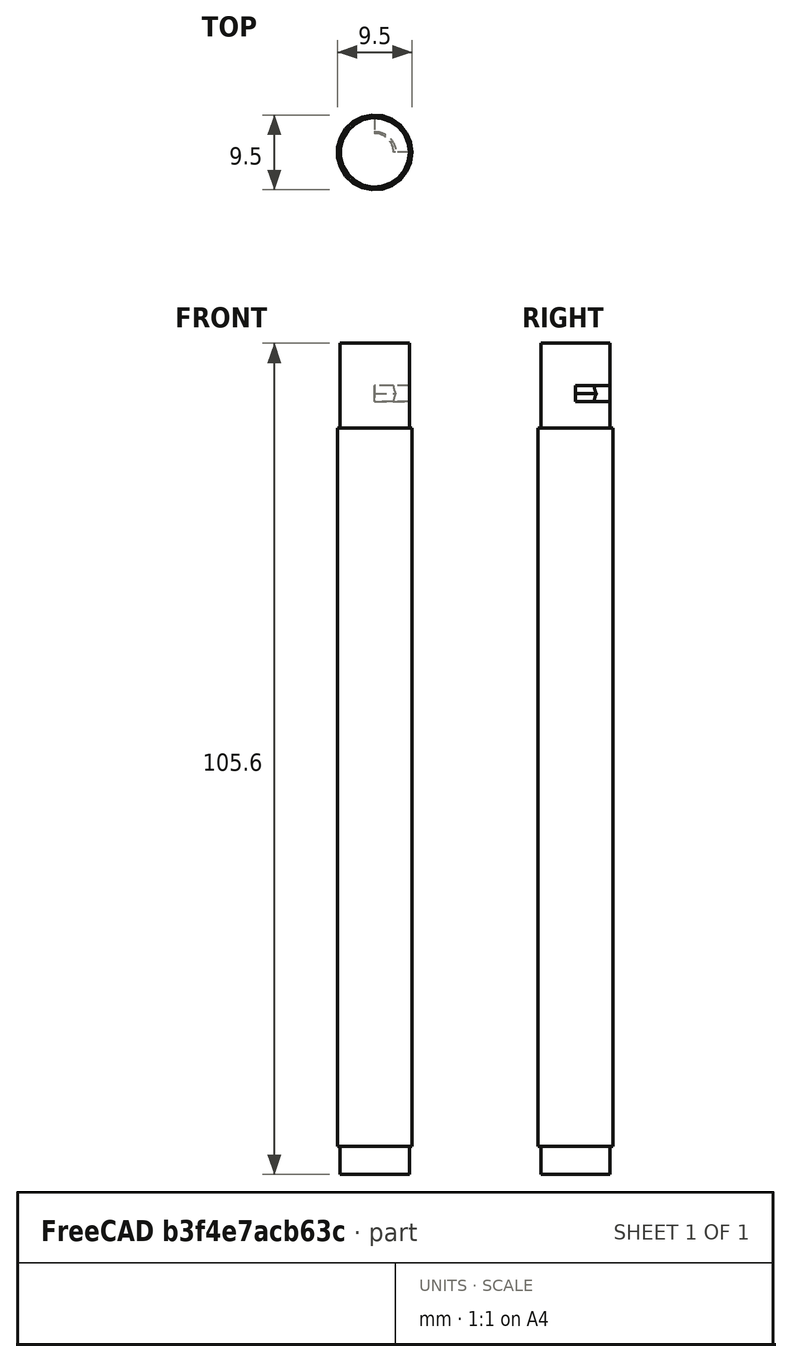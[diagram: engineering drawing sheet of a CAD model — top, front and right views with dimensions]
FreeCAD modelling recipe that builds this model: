
FCSTD DOCUMENT  (FreeCAD 0.20R29603 (Git))
Label: new_shaft
License: All rights reserved
LicenseURL: http://en.wikipedia.org/wiki/All_rights_reserved
objects: PartDesign::AdditiveCylinder×3, PartDesign::SubtractiveTorus×2, PartDesign::Body×1
note: 11 computed .brp shape members not serialized (recipe doc carries the construction recipe); baked Part::Feature solids carry a one-line shape summary decoded from their .brp

FEATURE [PartDesign::AdditiveCylinder] Cylinder
  Angle = 360
  AttacherType = Attacher::AttachEngine3D
  FirstAngle = 0
  Height = 91.2
  MapMode = 5
  Radius = 4.75
  SecondAngle = 0
  Support = -> [XY_Plane]
FEATURE [PartDesign::AdditiveCylinder] Cylinder001
  Angle = 360
  AttacherType = Attacher::AttachEngine3D
  BaseFeature = -> Cylinder
  FirstAngle = 0
  Height = 3.6
  MapMode = 5
  Placement = pos=(0,0,0) rot=(1,0,0;3.14159rad)
  Radius = 4.4
  SecondAngle = 0
  Support = -> [Cylinder]
FEATURE [PartDesign::AdditiveCylinder] Cylinder002
  Angle = 360
  AttacherType = Attacher::AttachEngine3D
  BaseFeature = -> Cylinder001
  FirstAngle = 0
  Height = 10.8
  MapMode = 5
  Placement = pos=(0,-1.12e-14,91.2) rot=(0,0,1;0rad)
  Radius = 4.4
  SecondAngle = 0
  Support = -> [Cylinder001]
FEATURE [PartDesign::SubtractiveTorus] Torus
  Angle1 = 0
  Angle2 = 180
  Angle3 = 90
  AttacherType = Attacher::AttachEngine3D
  BaseFeature = -> Cylinder002
  MapMode = 45
  Placement = pos=(0,-1.19e-14,96.6) rot=(0,0,1;0rad)
  Radius1 = 4.4
  Radius2 = 2
  Refine = true
  Support = -> [Cylinder002]
FEATURE [PartDesign::SubtractiveTorus] Torus001
  Angle1 = -180
  Angle2 = 0
  Angle3 = 90
  AttacherType = Attacher::AttachEngine3D
  AttachmentOffset = pos=(0,0,-2) rot=(0,0,1;0rad)
  BaseFeature = -> Torus
  MapMode = 45
  Placement = pos=(-1.3899e-12,-7.1e-14,94.6) rot=(0,0,1;0rad)
  Radius1 = 4.4
  Radius2 = 2
  Refine = true
  Support = -> [Cylinder002]
FEATURE [PartDesign::Body] Body
  Group = -> [Cylinder,Cylinder001,Cylinder002,Torus,Torus001]
  Origin = -> Origin
  Tip = -> Torus001
